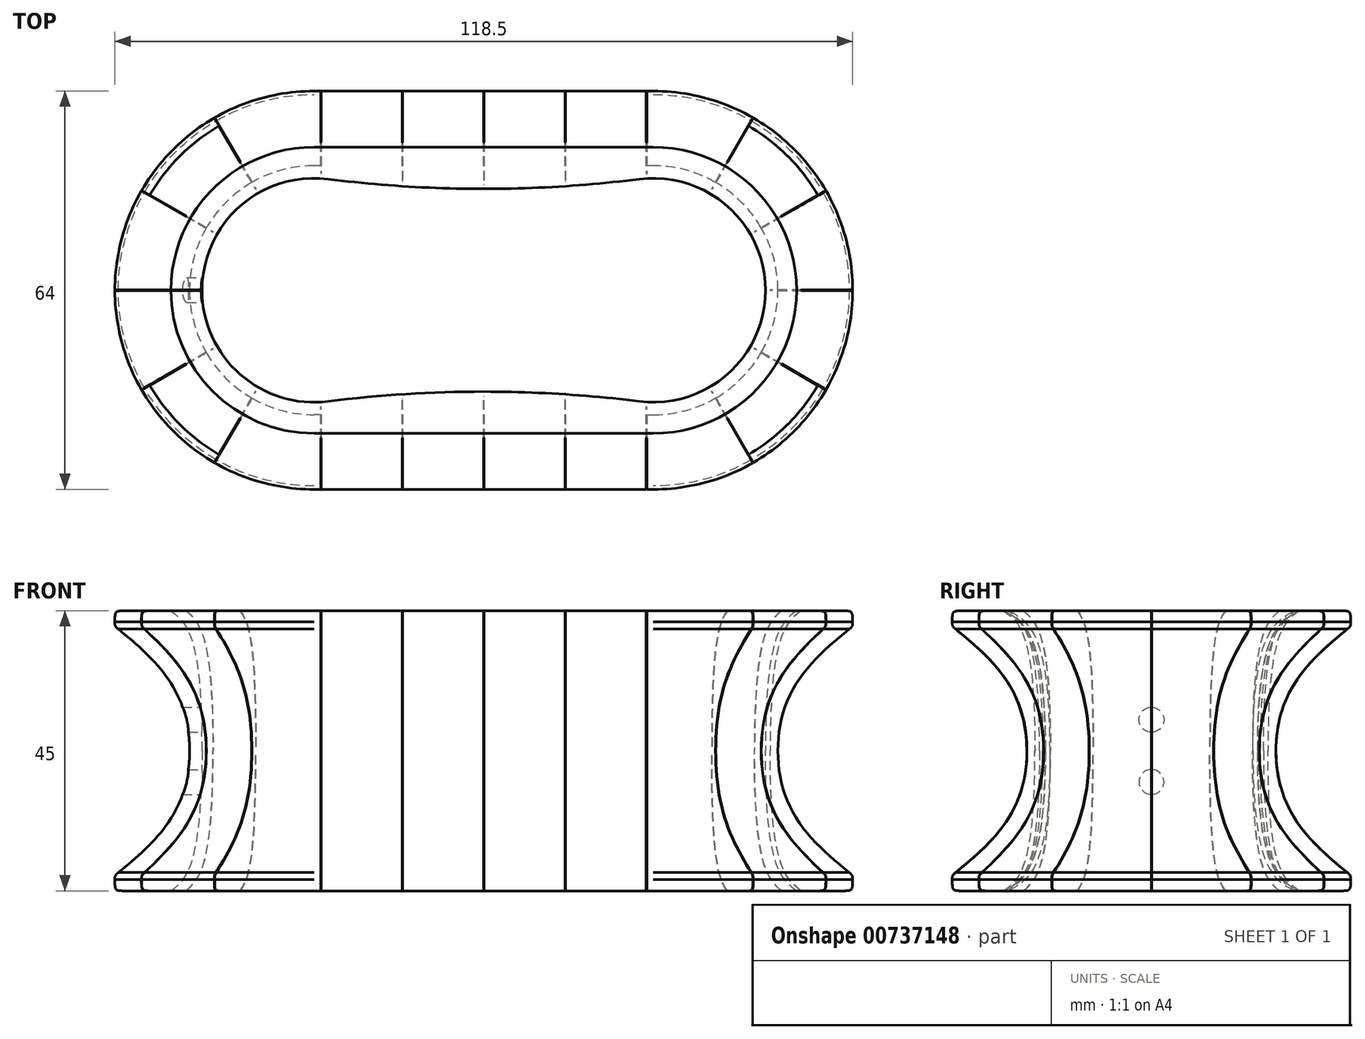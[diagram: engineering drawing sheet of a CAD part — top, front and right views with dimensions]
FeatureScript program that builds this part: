
annotation { "Feature Type Name" : "Feature", "Feature Type Description" : "" }
export const myFeature = defineFeature(function(context is Context, id is Id, definition is map)
    precondition{}
    {
        {
            var Q0;
            Q0=qCreatedBy(makeId("Top.planeOp"),FACE);
            var sketch = newSketch(context, id + "F0", { "sketchPlane" : qUnion([Q0])});
            skArc(sketch, "E0", {"start": v(-25, 17.86) * mm, "mid": v(0, 16.3) * mm, "end": v(25, 17.86) * mm});
            skArc(sketch, "E1", {"start": v(25, -17.86) * mm, "mid": v(45.25, 0) * mm, "end": v(25, 17.86) * mm});
            skArc(sketch, "E2", {"start": v(-25, 17.86) * mm, "mid": v(-45.25, 0) * mm, "end": v(-25, -17.86) * mm});
            skArc(sketch, "E3", {"start": v(25, -17.86) * mm, "mid": v(0, -16.3) * mm, "end": v(-25, -17.86) * mm});
            skLineSegment(sketch, "E4", {"start": v(-27.25, 0) * mm, "end": v(27.25, 0) * mm, "construction": true});
            skSolve(sketch);
        }
        {
            var Q0;
            Q0=qCreatedBy(makeId("Top.planeOp"),FACE);
            cPlane(context, id + "F1", {"entities" : qUnion([Q0]), "cplaneType" : CPlaneType.OFFSET, "offset" : 20 * mm, "width" : 150 * mm, "height" : 150 * mm});
        }
        {
            var Q0;
            Q0=qCreatedBy(makeId("Top.planeOp"),FACE);
            var sketch = newSketch(context, id + "F2", { "sketchPlane" : qUnion([Q0])});
            skArc(sketch, "E5", {"start": v(-27.25, 20) * mm, "mid": v(-47.25, 0) * mm, "end": v(-27.25, -20) * mm});
            skArc(sketch, "E6", {"start": v(27.25, -20) * mm, "mid": v(47.25, 0) * mm, "end": v(27.25, 20) * mm});
            skLineSegment(sketch, "E7", {"start": v(-27.25, 20) * mm, "end": v(27.25, 20) * mm});
            skLineSegment(sketch, "E8", {"start": v(27.25, -20) * mm, "end": v(-27.25, -20) * mm});
            skSolve(sketch);
        }
        {
            var Q0;
            Q0=qCreatedBy(id+"F1.planeOp",FACE);
            var sketch = newSketch(context, id + "F3", { "sketchPlane" : qUnion([Q0])});
            skLineSegment(sketch, "E9.0", {"start": v(-27.25, 32) * mm, "end": v(27.25, 32) * mm});
            skArc(sketch, "E9.1", {"start": v(-27.25, 32) * mm, "mid": v(-59.25, 0) * mm, "end": v(-27.25, -32) * mm});
            skLineSegment(sketch, "E9.2", {"start": v(27.25, -32) * mm, "end": v(-27.25, -32) * mm});
            skArc(sketch, "E9.3", {"start": v(27.25, -32) * mm, "mid": v(59.25, 0) * mm, "end": v(27.25, 32) * mm});
            skSolve(sketch);
        }
        {
            var Q0;
            Q0=makeQuery(id+"F2.imprint","IMPRINT",FACE,{"disambiguationData":[TD([[makeQuery(id+"F2.imprint","IMPRINT",EDGE,{"derivedFrom":sQuery(id+"F2.wireOp",EDGE,"E5")}),1.0]])]});
            var Q1;
            Q1=makeQuery(id+"F3.imprint","IMPRINT",FACE,{"disambiguationData":[TD([[makeQuery(id+"F3.imprint","IMPRINT",EDGE,{"derivedFrom":sQuery(id+"F3.wireOp",EDGE,"E9.0")}),-1.0]])]});
            loft(context, id + "F4", {"startCondition" : LoftEndDerivativeType.NORMAL_TO_PROFILE, "startMagnitude" : 1.5, "sheetProfilesArray" : [{ "sheetProfileEntities" : qUnion([Q0]) }, { "sheetProfileEntities" : qUnion([Q1]) }]});
        }
        {
            var Q0;
            Q0=makeQuery(id+"F4.opLoft","CAP_FACE",FACE,{"disambiguationData":[OSD([makeQuery(id+"F3.imprint","IMPRINT",FACE,{"disambiguationData":[TD([[makeQuery(id+"F3.imprint","IMPRINT",EDGE,{"derivedFrom":sQuery(id+"F3.wireOp",EDGE,"E9.0")}),-1.0]])]})])],"isStart":true});
            extrude(context, id + "F5", {"entities" : qUnion([Q0]), "operationType" : NewBodyOperationType.ADD, "depth" : 2.5 * mm, "offsetDistance" : 25 * mm});
        }
        {
            var Q0;
            Q0=makeQuery(id+"F5.opExtrude","CAP_FACE",FACE,{"disambiguationData":[OSD([makeQuery(id+"F3.imprint","IMPRINT",FACE,{"disambiguationData":[TD([[makeQuery(id+"F3.imprint","IMPRINT",EDGE,{"derivedFrom":sQuery(id+"F3.wireOp",EDGE,"E9.0")}),-1.0]])]})])],"isStart":false});
            var sketch = newSketch(context, id + "F6", { "sketchPlane" : qUnion([Q0])});
            skArc(sketch, "E10", {"start": v(-27.25, 23) * mm, "mid": v(-50.25, 0) * mm, "end": v(-27.25, -23) * mm});
            skArc(sketch, "E11", {"start": v(27.25, -23) * mm, "mid": v(50.25, 0) * mm, "end": v(27.25, 23) * mm});
            skLineSegment(sketch, "E12", {"start": v(-27.25, 23) * mm, "end": v(27.25, 23) * mm});
            skLineSegment(sketch, "E13", {"start": v(27.25, -23) * mm, "end": v(-27.25, -23) * mm});
            skSolve(sketch);
        }
        {
            var Q1;
            Q1=makeQuery(id+"F6.imprint","IMPRINT",FACE,{"disambiguationData":[TD([[makeQuery(id+"F6.imprint","IMPRINT",EDGE,{"derivedFrom":sQuery(id+"F6.wireOp",EDGE,"E10")}),1.0]])]});
            var Q2;
            Q2=makeQuery(id+"F0.imprint","IMPRINT",FACE,{"disambiguationData":[TD([[makeQuery(id+"F0.imprint","IMPRINT",EDGE,{"derivedFrom":sQuery(id+"F0.wireOp",EDGE,"E0")}),-1.0]])]});
            loft(context, id + "F7", {"operationType" : NewBodyOperationType.REMOVE, "endCondition" : LoftEndDerivativeType.NORMAL_TO_PROFILE, "endMagnitude" : 2.5, "sheetProfilesArray" : [{ "sheetProfileEntities" : qUnion([Q1]) }, { "sheetProfileEntities" : qUnion([Q2]) }]});
        }
        {
            var Q0;
            Q0=qCreatedBy(makeId("Top.planeOp"),FACE);
            var sketch = newSketch(context, id + "F8", { "sketchPlane" : qUnion([Q0])});
            skLineSegment(sketch, "E14", {"start": v(-65.05, 0) * mm, "end": v(-65.05, -15.33) * mm, "construction": true});
            skLineSegment(sketch, "E15", {"start": v(-65.05, -15.33) * mm, "end": v(-56.29, -30.51) * mm, "construction": true});
            skLineSegment(sketch, "E16", {"start": v(-56.29, -30.51) * mm, "end": v(-41.1, -39.28) * mm, "construction": true});
            skLineSegment(sketch, "E17", {"start": v(-41.1, -39.28) * mm, "end": v(22.99, -39.28) * mm, "construction": true});
            skSolve(sketch);
        }
        {
            var Q0;
            {var subQ0=sQuery(id+"F3.wireOp",EDGE,"E9.2");var subQ1=sQuery(id+"F3.wireOp",EDGE,"E9.1");var subQ2=sQuery(id+"F3.wireOp",EDGE,"E9.0");Q0=makeQuery(id+"F5.boolean.opBoolean","MERGE",EDGE,{"derivedFrom":[makeQuery(id+"F4.opLoft","MID_CAP_EDGE",EDGE,{"disambiguationData":[OSD([subQ2,subQ1,subQ0])],"capPos":1.0}),makeQuery(id+"F5.opExtrude","CAP_EDGE",EDGE,{"disambiguationData":[OSD([subQ2,subQ1,subQ0])],"isStart":true})]});}
            var Q1;
            Q1=makeQuery(id+"F5.opExtrude","CAP_EDGE",EDGE,{"disambiguationData":[OSD([sQuery(id+"F3.wireOp",EDGE,"E9.0"),sQuery(id+"F3.wireOp",EDGE,"E9.1"),sQuery(id+"F3.wireOp",EDGE,"E9.2")])],"isStart":false});
            fillet(context, id + "F9", {"entities" : qUnion([Q0, Q1]), "radius" : 1.5 * mm, "tangentPropagation" : true, "rho" : .7, "crossSection" : FilletCrossSection.CONIC, "allowEdgeOverflow" : false});
        }
        {
            var Q0;
            Q0=sQuery(id+"F8.wireOp",EDGE,"E14");
            cPlane(context, id + "F10", {"entities" : qUnion([Q0]), "cplaneType" : CPlaneType.LINE_ANGLE, "offset" : 25 * mm, "angle" : 90 * degree, "width" : 150 * mm, "height" : 150 * mm});
        }
        {
            var Q0;
            Q0=sQuery(id+"F8.wireOp",EDGE,"E15");
            cPlane(context, id + "F11", {"entities" : qUnion([Q0]), "cplaneType" : CPlaneType.LINE_ANGLE, "offset" : 25 * mm, "angle" : 90 * degree, "width" : 150 * mm, "height" : 150 * mm});
        }
        {
            var Q0;
            Q0=sQuery(id+"F8.wireOp",EDGE,"E16");
            cPlane(context, id + "F12", {"entities" : qUnion([Q0]), "cplaneType" : CPlaneType.LINE_ANGLE, "offset" : 90 * mm, "angle" : 0 * degree, "width" : 150 * mm, "height" : 150 * mm});
        }
        {
            var Q0;
            Q0=sQuery(id+"F8.wireOp",EDGE,"E17");
            cPlane(context, id + "F13", {"entities" : qUnion([Q0]), "cplaneType" : CPlaneType.LINE_ANGLE, "offset" : 25 * mm, "angle" : 0 * degree, "oppositeDirection" : true, "width" : 150 * mm, "height" : 150 * mm});
        }
        {
            var Q0;
            Q0=qCreatedBy(id+"F10.planeOp",FACE);
            var sketch = newSketch(context, id + "F14", { "sketchPlane" : qUnion([Q0])});
            skLineSegment(sketch, "E18.bottom", {"start": v(0.04, 0) * mm, "end": v(-0.04, 0) * mm});
            skLineSegment(sketch, "E18.top", {"start": v(0.04, 22.5) * mm, "end": v(-0.04, 22.5) * mm});
            skLineSegment(sketch, "E18.left", {"start": v(0.04, 0) * mm, "end": v(0.04, 22.5) * mm});
            skLineSegment(sketch, "E18.right", {"start": v(-0.04, 0) * mm, "end": v(-0.04, 22.5) * mm});
            skSolve(sketch);
        }
        {
            var Q0;
            Q0=qCreatedBy(id+"F11.planeOp",FACE);
            var sketch = newSketch(context, id + "F15", { "sketchPlane" : qUnion([Q0])});
            skLineSegment(sketch, "E19.bottom", {"start": v(13.66, 0) * mm, "end": v(13.59, 0) * mm});
            skLineSegment(sketch, "E19.top", {"start": v(13.66, 22.5) * mm, "end": v(13.59, 22.5) * mm});
            skLineSegment(sketch, "E19.left", {"start": v(13.66, 0) * mm, "end": v(13.66, 22.5) * mm});
            skLineSegment(sketch, "E19.right", {"start": v(13.59, 0) * mm, "end": v(13.59, 22.5) * mm});
            skSolve(sketch);
        }
        {
            var Q0;
            Q0=qCreatedBy(id+"F12.planeOp",FACE);
            var sketch = newSketch(context, id + "F16", { "sketchPlane" : qUnion([Q0])});
            skLineSegment(sketch, "E20.bottom", {"start": v(23.64, 0) * mm, "end": v(23.56, 0) * mm});
            skLineSegment(sketch, "E20.top", {"start": v(23.64, 22.5) * mm, "end": v(23.56, 22.5) * mm});
            skLineSegment(sketch, "E20.left", {"start": v(23.56, 0) * mm, "end": v(23.56, 22.5) * mm});
            skLineSegment(sketch, "E20.right", {"start": v(23.64, 0) * mm, "end": v(23.64, 22.5) * mm});
            skSolve(sketch);
        }
        {
            var Q0;
            Q0=qCreatedBy(id+"F13.planeOp",FACE);
            var sketch = newSketch(context, id + "F17", { "sketchPlane" : qUnion([Q0])});
            skLineSegment(sketch, "E21.bottom", {"start": v(0.04, 0) * mm, "end": v(-0.04, 0) * mm});
            skLineSegment(sketch, "E21.top", {"start": v(0.04, 22.5) * mm, "end": v(-0.04, 22.5) * mm});
            skLineSegment(sketch, "E21.left", {"start": v(0.04, 0) * mm, "end": v(0.04, 22.5) * mm});
            skLineSegment(sketch, "E21.right", {"start": v(-0.04, 0) * mm, "end": v(-0.04, 22.5) * mm});
            skLineSegment(sketch, "E22.bottom", {"start": v(13.04, 0) * mm, "end": v(13.11, 0) * mm});
            skLineSegment(sketch, "E22.top", {"start": v(13.04, 22.5) * mm, "end": v(13.11, 22.5) * mm});
            skLineSegment(sketch, "E22.left", {"start": v(13.04, 0) * mm, "end": v(13.04, 22.5) * mm});
            skLineSegment(sketch, "E22.right", {"start": v(13.11, 0) * mm, "end": v(13.11, 22.5) * mm});
            skLineSegment(sketch, "E23.bottom", {"start": v(26.11, 0) * mm, "end": v(26.19, 0) * mm});
            skLineSegment(sketch, "E23.top", {"start": v(26.11, 22.5) * mm, "end": v(26.19, 22.5) * mm});
            skLineSegment(sketch, "E23.left", {"start": v(26.11, 0) * mm, "end": v(26.11, 22.5) * mm});
            skLineSegment(sketch, "E23.right", {"start": v(26.19, 0) * mm, "end": v(26.19, 22.5) * mm});
            skLineSegment(sketch, "E24", {"start": v(26.11, 11.25) * mm, "end": v(13.11, 11.25) * mm, "construction": true});
            skLineSegment(sketch, "E25", {"start": v(13.04, 11.25) * mm, "end": v(0.04, 11.25) * mm, "construction": true});
            skSolve(sketch);
        }
        {
            var Q0;
            Q0 = qSketchRegion(id + "F14", true);
            var Q1;
            Q1=makeQuery(id+"F7.boolean.opBoolean","COPY",FACE,{"derivedFrom":makeQuery(id+"F7.opLoft","SWEPT_FACE",FACE,{"disambiguationData":[OSD([sQuery(id+"F0.wireOp",EDGE,"E0"),sQuery(id+"F0.wireOp",EDGE,"E1"),sQuery(id+"F0.wireOp",EDGE,"E2"),sQuery(id+"F6.wireOp",EDGE,"E10"),sQuery(id+"F6.wireOp",EDGE,"E11"),sQuery(id+"F6.wireOp",EDGE,"E12")])]})});
            extrude(context, id + "F18", {"entities" : qUnion([Q0]), "operationType" : NewBodyOperationType.REMOVE, "endBound" : BoundingType.UP_TO_SURFACE, "depth" : 25 * mm, "endBoundEntityFace" : qUnion([Q1]), "hasOffset" : true, "offsetDistance" : .75 * mm});
        }
        {
            var Q0;
            Q0=makeQuery(id+"F15.imprint","IMPRINT",FACE,{"disambiguationData":[TD([[makeQuery(id+"F15.imprint","IMPRINT",EDGE,{"derivedFrom":sQuery(id+"F15.wireOp",EDGE,"E19.bottom")}),-1.0]])]});
            var Q1;
            Q1=makeQuery(id+"F7.boolean.opBoolean","COPY",FACE,{"derivedFrom":makeQuery(id+"F7.opLoft","SWEPT_FACE",FACE,{"disambiguationData":[OSD([sQuery(id+"F0.wireOp",EDGE,"E0"),sQuery(id+"F0.wireOp",EDGE,"E1"),sQuery(id+"F0.wireOp",EDGE,"E2"),sQuery(id+"F6.wireOp",EDGE,"E10"),sQuery(id+"F6.wireOp",EDGE,"E11"),sQuery(id+"F6.wireOp",EDGE,"E12")])]})});
            extrude(context, id + "F19", {"entities" : qUnion([Q0]), "operationType" : NewBodyOperationType.REMOVE, "endBound" : BoundingType.UP_TO_SURFACE, "depth" : 25 * mm, "endBoundEntityFace" : qUnion([Q1]), "hasOffset" : true, "offsetDistance" : .75 * mm});
        }
        {
            var Q0;
            Q0=makeQuery(id+"F16.imprint","IMPRINT",FACE,{"disambiguationData":[TD([[makeQuery(id+"F16.imprint","IMPRINT",EDGE,{"derivedFrom":sQuery(id+"F16.wireOp",EDGE,"E20.bottom")}),-1.0]])]});
            var Q1;
            Q1 = qConstructionFilter(qBodyType(qCreatedBy(id + "F16" ,EDGE), BodyType.WIRE), ConstructionObject.NO);
            var Q2;
            Q2=makeQuery(id+"F7.boolean.opBoolean","COPY",FACE,{"derivedFrom":makeQuery(id+"F7.opLoft","SWEPT_FACE",FACE,{"disambiguationData":[OSD([sQuery(id+"F0.wireOp",EDGE,"E0"),sQuery(id+"F0.wireOp",EDGE,"E1"),sQuery(id+"F0.wireOp",EDGE,"E2"),sQuery(id+"F6.wireOp",EDGE,"E10"),sQuery(id+"F6.wireOp",EDGE,"E11"),sQuery(id+"F6.wireOp",EDGE,"E12")])]})});
            extrude(context, id + "F20", {"entities" : qUnion([Q0]), "operationType" : NewBodyOperationType.REMOVE, "surfaceEntities" : qUnion([Q1]), "endBound" : BoundingType.UP_TO_SURFACE, "depth" : 25 * mm, "endBoundEntityFace" : qUnion([Q2]), "hasOffset" : true, "offsetDistance" : .75 * mm});
        }
        {
            var Q0;
            Q0 = qSketchRegion(id + "F17", true);
            var Q1;
            Q1=makeQuery(id+"F7.boolean.opBoolean","COPY",FACE,{"derivedFrom":makeQuery(id+"F7.opLoft","SWEPT_FACE",FACE,{"disambiguationData":[OSD([sQuery(id+"F0.wireOp",EDGE,"E0"),sQuery(id+"F0.wireOp",EDGE,"E1"),sQuery(id+"F0.wireOp",EDGE,"E2"),sQuery(id+"F6.wireOp",EDGE,"E10"),sQuery(id+"F6.wireOp",EDGE,"E11"),sQuery(id+"F6.wireOp",EDGE,"E12")])]})});
            extrude(context, id + "F21", {"entities" : qUnion([Q0]), "operationType" : NewBodyOperationType.REMOVE, "endBound" : BoundingType.UP_TO_SURFACE, "depth" : 25 * mm, "endBoundEntityFace" : qUnion([Q1]), "hasOffset" : true, "offsetDistance" : .75 * mm});
        }
        {
            var Q0;
            Q0=qCreatedBy(makeId("Top.planeOp"),FACE);
            var sketch = newSketch(context, id + "F22", { "sketchPlane" : qUnion([Q0])});
            skLineSegment(sketch, "E26", {"start": v(0, 0) * mm, "end": v(0, -60) * mm});
            skLineSegment(sketch, "E27", {"start": v(0, -60) * mm, "end": v(120, -60) * mm});
            skLineSegment(sketch, "E28", {"start": v(120, -60) * mm, "end": v(120, 60) * mm});
            skLineSegment(sketch, "E29", {"start": v(120, 60) * mm, "end": v(-120, 60) * mm});
            skLineSegment(sketch, "E30", {"start": v(-120, 60) * mm, "end": v(-120, 0) * mm});
            skLineSegment(sketch, "E31", {"start": v(-120, 0) * mm, "end": v(0, 0) * mm});
            skSolve(sketch);
        }
        {
            var Q0;
            Q0 = qSketchRegion(id + "F22", true);
            extrude(context, id + "F23", {"entities" : qUnion([Q0]), "operationType" : NewBodyOperationType.REMOVE, "endBound" : BoundingType.THROUGH_ALL, "depth" : 25 * mm, "offsetDistance" : 25 * mm});
        }
        {
            var Q0;
            Q0=makeQuery(id+"F4.opLoft","SWEPT_BODY",BODY,{"disambiguationData":[OSD([makeQuery(id+"F2.imprint","IMPRINT",FACE,{"disambiguationData":[TD([[makeQuery(id+"F2.imprint","IMPRINT",EDGE,{"derivedFrom":sQuery(id+"F2.wireOp",EDGE,"E5")}),1.0]])]}),makeQuery(id+"F3.imprint","IMPRINT",FACE,{"disambiguationData":[TD([[makeQuery(id+"F3.imprint","IMPRINT",EDGE,{"derivedFrom":sQuery(id+"F3.wireOp",EDGE,"E9.0")}),-1.0]])]})])]});
            var Q1;
            Q1=makeQuery(id+"F23.boolean.opBoolean","COPY",FACE,{"derivedFrom":makeQuery(id+"F23.opExtrude","SWEPT_FACE",FACE,{"disambiguationData":[OSD([sQuery(id+"F22.wireOp",EDGE,"E26")])]})});
            mirror(context, id + "F24", {"operationType" : NewBodyOperationType.ADD, "entities" : qUnion([Q0]), "mirrorPlane" : qUnion([Q1])});
        }
        {
            var Q0;
            Q0=makeQuery(id+"F4.opLoft","SWEPT_BODY",BODY,{"disambiguationData":[OSD([makeQuery(id+"F2.imprint","IMPRINT",FACE,{"disambiguationData":[TD([[makeQuery(id+"F2.imprint","IMPRINT",EDGE,{"derivedFrom":sQuery(id+"F2.wireOp",EDGE,"E5")}),1.0]])]}),makeQuery(id+"F3.imprint","IMPRINT",FACE,{"disambiguationData":[TD([[makeQuery(id+"F3.imprint","IMPRINT",EDGE,{"derivedFrom":sQuery(id+"F3.wireOp",EDGE,"E9.0")}),-1.0]])]})])]});
            var Q1;
            Q1=makeQuery(id+"F24.opPattern","COPY",FACE,{"derivedFrom":makeQuery(id+"F23.boolean.opBoolean","COPY",FACE,{"derivedFrom":makeQuery(id+"F23.opExtrude","SWEPT_FACE",FACE,{"disambiguationData":[OSD([sQuery(id+"F22.wireOp",EDGE,"E31")])]})}),"instanceName":"1"});
            mirror(context, id + "F25", {"operationType" : NewBodyOperationType.ADD, "entities" : qUnion([Q0]), "mirrorPlane" : qUnion([Q1])});
        }
        {
            var Q0;
            Q0=qCreatedBy(makeId("Right.planeOp"),FACE);
            var sketch = newSketch(context, id + "F26", { "sketchPlane" : qUnion([Q0])});
            skLineSegment(sketch, "E32.bottom", {"start": v(0.04, 0) * mm, "end": v(-0.04, 0) * mm});
            skLineSegment(sketch, "E32.top", {"start": v(0.04, 22.5) * mm, "end": v(-0.04, 22.5) * mm});
            skLineSegment(sketch, "E32.left", {"start": v(0.04, 0) * mm, "end": v(0.04, 22.5) * mm});
            skLineSegment(sketch, "E32.right", {"start": v(-0.04, 0) * mm, "end": v(-0.04, 22.5) * mm});
            skCircle(sketch, "E33", {"center": v(0, 5) * mm, "radius": 2 * mm});
            skSolve(sketch);
        }
        {
            var Q0;
            Q0 = qSketchRegion(id + "F26", true);
            extrude(context, id + "F27", {"entities" : qUnion([Q0]), "operationType" : NewBodyOperationType.REMOVE, "endBound" : BoundingType.THROUGH_ALL, "oppositeDirection" : true, "depth" : 25 * mm, "offsetDistance" : 25 * mm});
        }
        {
            var Q0;
            Q0=makeQuery(id+"F4.opLoft","SWEPT_BODY",BODY,{"disambiguationData":[OSD([makeQuery(id+"F2.imprint","IMPRINT",FACE,{"disambiguationData":[TD([[makeQuery(id+"F2.imprint","IMPRINT",EDGE,{"derivedFrom":sQuery(id+"F2.wireOp",EDGE,"E5")}),1.0]])]}),makeQuery(id+"F3.imprint","IMPRINT",FACE,{"disambiguationData":[TD([[makeQuery(id+"F3.imprint","IMPRINT",EDGE,{"derivedFrom":sQuery(id+"F3.wireOp",EDGE,"E9.0")}),-1.0]])]})])]});
            var Q1;
            {var subQ0=makeQuery(id+"F4.opLoft","CAP_FACE",FACE,{"disambiguationData":[OSD([makeQuery(id+"F2.imprint","IMPRINT",FACE,{"disambiguationData":[TD([[makeQuery(id+"F2.imprint","IMPRINT",EDGE,{"derivedFrom":sQuery(id+"F2.wireOp",EDGE,"E5")}),1.0]])]})])],"isStart":true});var subQ1=makeQuery(id+"F24.boolean.opBoolean","MERGE",FACE,{"derivedFrom":[subQ0,makeQuery(id+"F24.opPattern","COPY",FACE,{"derivedFrom":subQ0,"instanceName":"1"})]});Q1=makeQuery(id+"F25.boolean.opBoolean","MERGE",FACE,{"derivedFrom":[subQ1,makeQuery(id+"F25.opPattern","COPY",FACE,{"derivedFrom":subQ1,"instanceName":"1"})]});}
            mirror(context, id + "F28", {"operationType" : NewBodyOperationType.ADD, "entities" : qUnion([Q0]), "mirrorPlane" : qUnion([Q1])});
        }
    });
